# Revit family: Поли-Групп_ЗадвижкаКлиноваяEAZ-МК-F5(ВS)_DN40-300
name_source: partatom
category: Арматура трубопроводов
units: mm (PartAtom-declared; Revit-internal decimal feet)

## family parameters
Всегда вертикально = Да
На основе рабочей плоскости = Нет
Общий = Нет
При загрузке вырезать с полостями = Нет
Размер круглого соединителя = Использовать диаметр
Тип детали = Клапан - Вставляется

## types (13) — shared parameters
ADSK_URL страницы изделия = https://www.polycorr.ru
ADSK_Версия Revit = 2019
ADSK_Единица измерения = шт
ADSK_Завод-изготовитель = ООО ПК «Поли-Групп»
ADSK_Количество = 1
ADSK_Материал = Высокопрочный чугун GGG-40
ADSK_Материал наименование = Высокопрочный чугун с шаровидным графитом (GGG-40)
Kv = 1.0 м³/ч
Класс герметичности = А по ГОСТ Р 9544-2015
Материал Диска = Высокопрочный чугун с шаровидным графитом (GGG-40)
Материал уплотнителя = PTFE
Назначение = Для установки в качестве запорного устройства на трубопроводах
Покрытие = Высококачественное эпоксидное покрытие толщиной 300 мкм
Рабочая среда = Техническая вода, канализационные стоки, морская вода
Разработчик = https://3dbim.pro
Срок службы = 50 лет
ТВ = Поли-Групп_ЗадвижкаКлиноваяEAZ-МК-F5(ВS)_DN40-300
Температура рабочей среды = 0 до +70°С
Тип привода = Штурвал
Тип присоединения = Фланцевое

## per-type parameters (varying)
| type | A | ADSK_Марка | ADSK_Масса | ADSK_Масса_Текст | ADSK_Наименование | ADSK_Наименование краткое | D | D2 | DN | DO | D_Наружный | H2 | L | PN | R | b | d1 | f | h2 | l1 | l2 | l3 | t | Габаритные размеры |
| 40-16 | 135 мм | EAZ-GV-3-F5 DN40 PN16 | 11 | 11 | Задвижка клиновая с металлическим уплотнением EAZ MK F5 для сточных вод фланцевая DN40 PN16 | Задвижка клиновая EAZ MK F5 DN40 PN16 | 150 мм | 84 мм | 40 мм | 160 мм | 49 мм | 245 мм | 240 мм | 16.0 бары | 10 мм | 16 мм | 10 мм | 3 мм | 123 мм | 144 мм | 156 мм | 216 мм | 12 мм | 150х240х320 |
| 50-16 | 149 мм | EAZ-GV-3-F5 DN50 PN16 | 13 | 13 | Задвижка клиновая с металлическим уплотнением EAZ MK F5 для сточных вод фланцевая DN50 PN16 | Задвижка клиновая EAZ MK F5 DN50 PN16 | 165 мм | 99 мм | 50 мм | 160 мм | 59 мм | 255 мм | 250 мм | 16.0 бары | 10 мм | 16 мм | 13 мм | 3 мм | 128 мм | 150 мм | 163 мм | 225 мм | 13 мм | 165х250х338 |
| 65-16 | 167 мм | EAZ-GV-3-F5 DN65 PN16 | 16 | 16 | Задвижка клиновая с металлическим уплотнением EAZ MK F5 для сточных вод фланцевая DN65 PN16 | Задвижка клиновая EAZ MK F5 DN65 PN16 | 185 мм | 118 мм | 65 мм | 160 мм | 74 мм | 277 мм | 270 мм | 16.0 бары | 10 мм | 16 мм | 16 мм | 3 мм | 139 мм | 162 мм | 176 мм | 243 мм | 14 мм | 185х270х370 |
| 80-16 | 180 мм | EAZ-GV-3-F5 DN80 PN16 | 20 | 20 | Задвижка клиновая с металлическим уплотнением EAZ MK F5 для сточных вод фланцевая DN80 PN16 | Задвижка клиновая EAZ MK F5 DN80 PN16 | 200 мм | 132 мм | 80 мм | 160 мм | 89 мм | 304 мм | 280 мм | 16.0 бары | 10 мм | 17 мм | 20 мм | 3 мм | 152 мм | 168 мм | 182 мм | 252 мм | 15 мм | 200х280х404 |
| 100-16 | 198 мм | EAZ-GV-3-F5 DN100 PN16 | 27 | 27 | Задвижка клиновая с металлическим уплотнением EAZ MK F5 для сточных вод фланцевая DN100 PN16 | Задвижка клиновая EAZ MK F5 DN100 PN16 | 220 мм | 156 мм | 100 мм | 200 мм | 109 мм | 332 мм | 300 мм | 16.0 бары | 11 мм | 17 мм | 25 мм | 3 мм | 166 мм | 180 мм | 195 мм | 270 мм | 17 мм | 220х300х442 |
| 125-16 | 225 мм | EAZ-GV-3-F5 DN125 PN16 | 38 | 38 | Задвижка клиновая с металлическим уплотнением EAZ MK F5 для сточных вод фланцевая DN125 PN16 | Задвижка клиновая EAZ MK F5 DN125 PN16 | 250 мм | 184 мм | 125 мм | 200 мм | 134 мм | 388 мм | 325 мм | 16.0 бары | 11 мм | 18 мм | 31 мм | 3 мм | 194 мм | 195 мм | 211 мм | 293 мм | 19 мм | 250х325х513 |
| 150-16 | 257 мм | EAZ-GV-3-F5 DN150 PN16 | 43 | 43 | Задвижка клиновая с металлическим уплотнением EAZ MK F5 для сточных вод фланцевая DN150 PN16 | Задвижка клиновая EAZ MK F5 DN150 PN16 | 285 мм | 211 мм | 150 мм | 250 мм | 159 мм | 455 мм | 350 мм | 16.0 бары | 11 мм | 20 мм | 38 мм | 3 мм | 228 мм | 210 мм | 228 мм | 315 мм | 23 мм | 285х350х598 |
| 200-16 | 306 мм | EAZ-GV-3-F5 DN200 PN16 | 75 | 75 | Задвижка клиновая с металлическим уплотнением EAZ MK F5 для сточных вод фланцевая DN200 PN16 | Задвижка клиновая EAZ MK F5 DN200 PN16 | 340 мм | 266 мм | 200 мм | 250 мм | 209 мм | 538 мм | 400 мм | 16.0 бары | 13 мм | 21 мм | 50 мм | 3 мм | 269 мм | 240 мм | 260 мм | 360 мм | 27 мм | 340х400х708 |
| 250-16 | 365 мм | EAZ-GV-3-F5 DN250 PN16 | 114 | 114 | Задвижка клиновая с металлическим уплотнением EAZ MK F5 для сточных вод фланцевая DN250 PN16 | Задвижка клиновая EAZ MK F5 DN250 PN16 | 405 мм | 319 мм | 250 мм | 320 мм | 259 мм | 629 мм | 450 мм | 16.0 бары | 15 мм | 23 мм | 63 мм | 3 мм | 315 мм | 270 мм | 293 мм | 405 мм | 31 мм | 405х450х832 |
| 300-16 | 414 мм | EAZ-GV-3-F5 DN300 PN16 | 160 | 160 | Задвижка клиновая с металлическим уплотнением EAZ MK F5 для сточных вод фланцевая DN300 PN16 | Задвижка клиновая EAZ MK F5 DN300 PN16 | 460 мм | 370 мм | 300 мм | 320 мм | 309 мм | 730 мм | 500 мм | 16.0 бары | 17 мм | 24 мм | 75 мм | 4 мм | 365 мм | 300 мм | 325 мм | 450 мм | 37 мм | 460х500х960 |
| 200-10 | 306 мм | EAZ-GV-3-F5 DN200 PN10 | 75 | 75 | Задвижка клиновая с металлическим уплотнением EAZ MK F5 для сточных вод фланцевая DN200 PN10 | Задвижка клиновая EAZ MK F5 DN200 PN10 | 340 мм | 266 мм | 200 мм | 250 мм | 209 мм | 538 мм | 400 мм | 10.0 бары | 13 мм | 21 мм | 50 мм | 3 мм | 269 мм | 240 мм | 260 мм | 360 мм | 27 мм | 340х400х708 |
| 250-10 | 365 мм | EAZ-GV-3-F5 DN250 PN10 | 115 | 115 | Задвижка клиновая с металлическим уплотнением EAZ MK F5 для сточных вод фланцевая DN250 PN10 | Задвижка клиновая EAZ MK F5 DN250 PN10 | 405 мм | 319 мм | 250 мм | 320 мм | 259 мм | 629 мм | 450 мм | 10.0 бары | 15 мм | 23 мм | 63 мм | 3 мм | 315 мм | 270 мм | 293 мм | 405 мм | 31 мм | 405х450х832 |
| 300-10 | 414 мм | EAZ-GV-3-F5 DN300 PN10 | 155 | 155 | Задвижка клиновая с металлическим уплотнением EAZ MK F5 для сточных вод фланцевая DN300 PN10 | Задвижка клиновая EAZ MK F5 DN300 PN10 | 460 мм | 370 мм | 300 мм | 320 мм | 309 мм | 730 мм | 500 мм | 10.0 бары | 17 мм | 24 мм | 75 мм | 4 мм | 365 мм | 300 мм | 325 мм | 450 мм | 37 мм | 460х500х960 |
